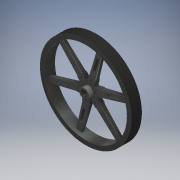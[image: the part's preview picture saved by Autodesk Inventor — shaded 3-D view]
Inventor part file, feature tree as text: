
AUTODESK INVENTOR PART (.ipt)
format: ipt  version: 2019 (Build 230136000, 136)  size: 580,096 bytes
history: mixed  units: in
note: dims shown in document units (in); Inventor stores cm internally (conversion verified against a paired STEP export)
features: fillet x1, imported_body x1
ambient origin geometry x8: Origin, YZ Plane, XZ Plane, XY Plane, X Axis, Y Axis, Z Axis, Center Point
bodies: Solid1 (imported_parasolid)
feature tree (2):
  fillet  "Fillet18"  [1 undecoded]
  imported_body  NMx_Import_Brep_tag  [imported B-rep: ~24 faces, bbox_mm=[11.957142, 12.33927, 4.0]]
note: 1 required parameter value undecoded (feature->parameter linkage not recoverable at this tier; creation-order binding heuristic only, values carry confidence <= 0.55)
